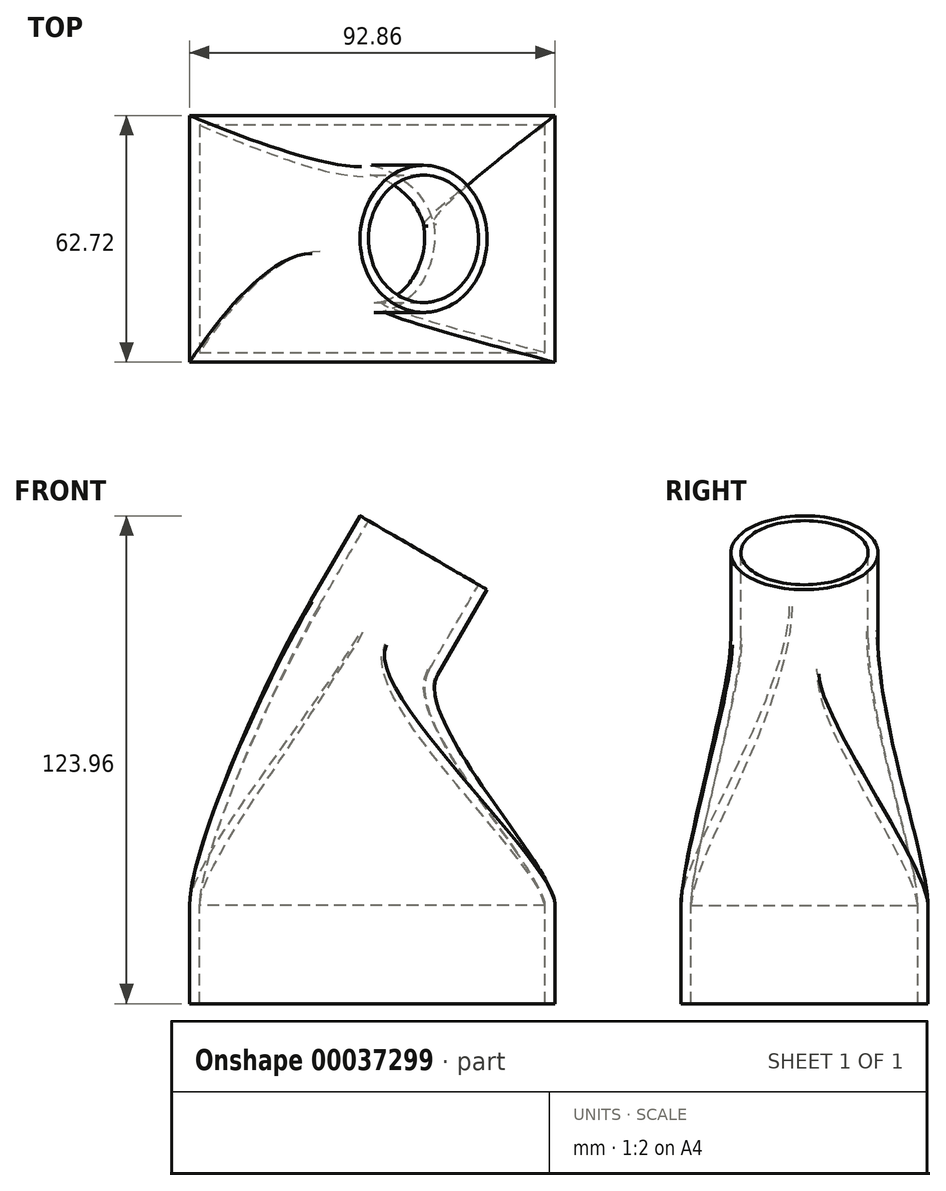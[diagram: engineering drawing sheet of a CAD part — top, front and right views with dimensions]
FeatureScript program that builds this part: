
annotation { "Feature Type Name" : "Feature", "Feature Type Description" : "" }
export const myFeature = defineFeature(function(context is Context, id is Id, definition is map)
    precondition{}
    {
        {
            var Q0;
            Q0=qCreatedBy(makeId("Top.planeOp"),FACE);
            var sketch = newSketch(context, id + "F0", { "sketchPlane" : qUnion([Q0])});
            skLineSegment(sketch, "E0.rect.bottom", {"start": v(-46.43, 31.36) * mm, "end": v(46.43, 31.36) * mm});
            skLineSegment(sketch, "E0.rect.top", {"start": v(-46.43, -31.36) * mm, "end": v(46.43, -31.36) * mm});
            skLineSegment(sketch, "E0.rect.left", {"start": v(-46.43, 31.36) * mm, "end": v(-46.43, -31.36) * mm});
            skLineSegment(sketch, "E0.rect.right", {"start": v(46.43, 31.36) * mm, "end": v(46.43, -31.36) * mm});
            skPoint(sketch, "E0.rect.middle", {"position": v(0, 0) * mm});
            skSolve(sketch);
        }
        {
            var Q0;
            Q0=qCreatedBy(makeId("Front.planeOp"),FACE);
            var sketch = newSketch(context, id + "F1", { "sketchPlane" : qUnion([Q0])});
            skLineSegment(sketch, "E1", {"start": v(-37.39, 89.98) * mm, "end": v(86.42, 17.94) * mm, "construction": true});
            skSolve(sketch);
        }
        {
            var Q0;
            Q0=sQuery(id+"F1.wireOp",EDGE,"E1");
            cPlane(context, id + "F2", {"entities" : qUnion([Q0]), "cplaneType" : CPlaneType.LINE_ANGLE, "offset" : 150 * mm, "angle" : 90 * degree, "width" : 150 * mm, "height" : 150 * mm});
        }
        {
            var Q0;
            Q0=qCreatedBy(id+"F2.planeOp",FACE);
            var sketch = newSketch(context, id + "F3", { "sketchPlane" : qUnion([Q0])});
            skCircle(sketch, "E2", {"center": v(-33.78, 0) * mm, "radius": 18.68 * mm});
            skSolve(sketch);
        }
        {
            var Q0;
            Q0=makeQuery(id+"F0.imprint","IMPRINT",FACE,{"disambiguationData":[TD([[makeQuery(id+"F0.imprint","IMPRINT",EDGE,{"derivedFrom":sQuery(id+"F0.wireOp",EDGE,"E0.rect.bottom")}),-1.0]])]});
            var Q1;
            Q1=makeQuery(id+"F3.imprint","IMPRINT",FACE,{"disambiguationData":[TD([[makeQuery(id+"F3.imprint","IMPRINT",EDGE,{"derivedFrom":sQuery(id+"F3.wireOp",EDGE,"E2")}),1.0]])]});
            loft(context, id + "F4", {"startCondition" : LoftEndDerivativeType.NORMAL_TO_PROFILE, "startMagnitude" : .5, "endCondition" : LoftEndDerivativeType.NORMAL_TO_PROFILE, "endMagnitude" : 1, "sheetProfilesArray" : [{ "sheetProfileEntities" : qUnion([Q0]) }, { "sheetProfileEntities" : qUnion([Q1]) }]});
        }
        {
            var Q0;
            Q0=makeQuery(id+"F4.opLoft","CAP_FACE",FACE,{"disambiguationData":[OSD([makeQuery(id+"F3.imprint","IMPRINT",FACE,{"disambiguationData":[TD([[makeQuery(id+"F3.imprint","IMPRINT",EDGE,{"derivedFrom":sQuery(id+"F3.wireOp",EDGE,"E2")}),1.0]])]})])],"isStart":true});
            extrude(context, id + "F5", {"entities" : qUnion([Q0]), "operationType" : NewBodyOperationType.ADD, "depth" : 25 * mm});
        }
        {
            var Q0;
            Q0=makeQuery(id+"F4.opLoft","CAP_FACE",FACE,{"disambiguationData":[OSD([makeQuery(id+"F0.imprint","IMPRINT",FACE,{"disambiguationData":[TD([[makeQuery(id+"F0.imprint","IMPRINT",EDGE,{"derivedFrom":sQuery(id+"F0.wireOp",EDGE,"E0.rect.bottom")}),-1.0]])]})])],"isStart":true});
            extrude(context, id + "F6", {"entities" : qUnion([Q0]), "operationType" : NewBodyOperationType.ADD, "depth" : 25 * mm});
        }
        {
            var Q0;
            Q0=makeQuery(id+"F6.opExtrude","CAP_FACE",FACE,{"disambiguationData":[OSD([makeQuery(id+"F0.imprint","IMPRINT",FACE,{"disambiguationData":[TD([[makeQuery(id+"F0.imprint","IMPRINT",EDGE,{"derivedFrom":sQuery(id+"F0.wireOp",EDGE,"E0.rect.bottom")}),-1.0]])]})])],"isStart":false});
            var Q1;
            Q1=makeQuery(id+"F5.opExtrude","CAP_FACE",FACE,{"disambiguationData":[OSD([makeQuery(id+"F3.imprint","IMPRINT",FACE,{"disambiguationData":[TD([[makeQuery(id+"F3.imprint","IMPRINT",EDGE,{"derivedFrom":sQuery(id+"F3.wireOp",EDGE,"E2")}),1.0]])]})])],"isStart":false});
            shell(context, id + "F7", {"entities" : qUnion([Q0, Q1]), "thickness" : 2.5 * mm});
        }
    });
